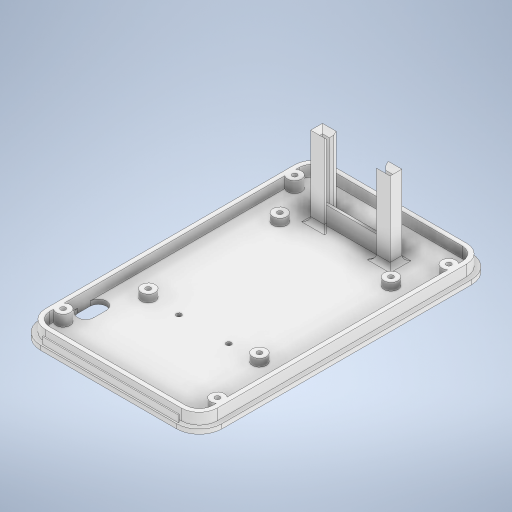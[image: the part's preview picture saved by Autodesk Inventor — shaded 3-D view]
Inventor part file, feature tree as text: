
AUTODESK INVENTOR PART (.ipt)
format: ipt  version: 2023 (Build 270158000, 158)  size: 502,272 bytes
history: native  units: mm
features: extrude x12, sketch x9, fillet x1
ambient origin geometry x8: Origin, YZ Plane, XZ Plane, XY Plane, X Axis, Y Axis, Z Axis, Center Point
bodies: Solid1 (feature_tree)
feature tree (22):
  extrude  "Extrusion1"  Depth=130.0mm
  extrude  "Extrusion2"  TaperAngle=0.0deg  [1 undecoded]
  sketch  "Sketch4"  dims[d4=10.0mm d11=2.1mm]
  extrude  "Extrusion3"  Depth=2.1mm
  extrude  "Extrusion4"  Depth=2.1mm
  extrude  "Extrusion5"  Depth=7.9mm
  extrude  "Extrusion6"  Depth=4.9mm
  extrude  "Extrusion8"  Depth=2.2mm
  sketch  "Sketch7"  dims[d16=2.0mm d17=4.9mm]
  extrude  "Extrusion9"  Depth=6.0mm
  extrude  "Extrusion10"  Depth=10.0mm
  extrude  "Extrusion11"  Depth=4.9mm
  fillet  "Fillet1"  [1 undecoded]
  extrude  "Extrusion12"  Depth=4.9mm
  extrude  "Extrusion13"  TaperAngle=0.0deg  [1 undecoded]
  sketch  "Sketch1"  dims[d0=80.0mm d1=130.0mm]
  sketch  "Sketch3"  dims[d2=2.0mm d3=0.0mm]
  sketch  "Sketch5"  dims[d12=2.1mm d13=2.1mm]
  sketch  "Sketch6"  dims[d14=2.1mm d15=7.9mm]
  sketch  "Sketch8"  dims[d18=0.0mm d20=2.2mm]
  sketch  "Sketch9"  dims[d21=14.0mm d22=6.0mm]
  sketch  "Sketch10"  dims[d23=20.0mm d25=102.0mm d26=20.0mm d28=68.0mm d31=4.9mm d32=0.0mm d33=4.9mm d34=0.0mm d35=2.0mm d36=4.2mm d37=14.0mm d38=6.0mm d39=20.0mm d41=68.0mm d42=20.0mm d44=102.0mm d47=2.1mm d48=0.0mm d49=4.2mm d50=20.0mm d52=58.0mm d53=20.0mm d55=49.0mm d58=42.0mm d59=2.2mm d60=2.0mm d61=20.0mm d63=58.0mm d64=20.0mm d66=49.0mm d69=42.0mm d70=3.3mm d71=0.0mm d72=2.2mm d73=2.2mm d74=22.0mm d75=42.0mm d78=3.3mm d79=0.0mm d84=1.0mm d89=1.0mm d90=2.0mm d91=2.0mm d92=2.0mm d93=31.0mm d94=1.2mm d95=135.0deg d96=135.0deg d97=21.4mm d98=35.0mm d99=0.0mm d100=7.9mm d101=0.0mm d102=2.0mm d103=-7.853982mm d104=4.0mm d105=2.0mm d106=0.5mm d107=10.2mm d108=10.0mm d109=0.7mm d110=3.0mm d111=0.0mm d112=12.7mm d113=7.2mm d114=10.0mm d115=0.0mm d117=25.0mm]
note: 3 required parameter values undecoded (feature->parameter linkage not recoverable at this tier; creation-order binding heuristic only, values carry confidence <= 0.55)
